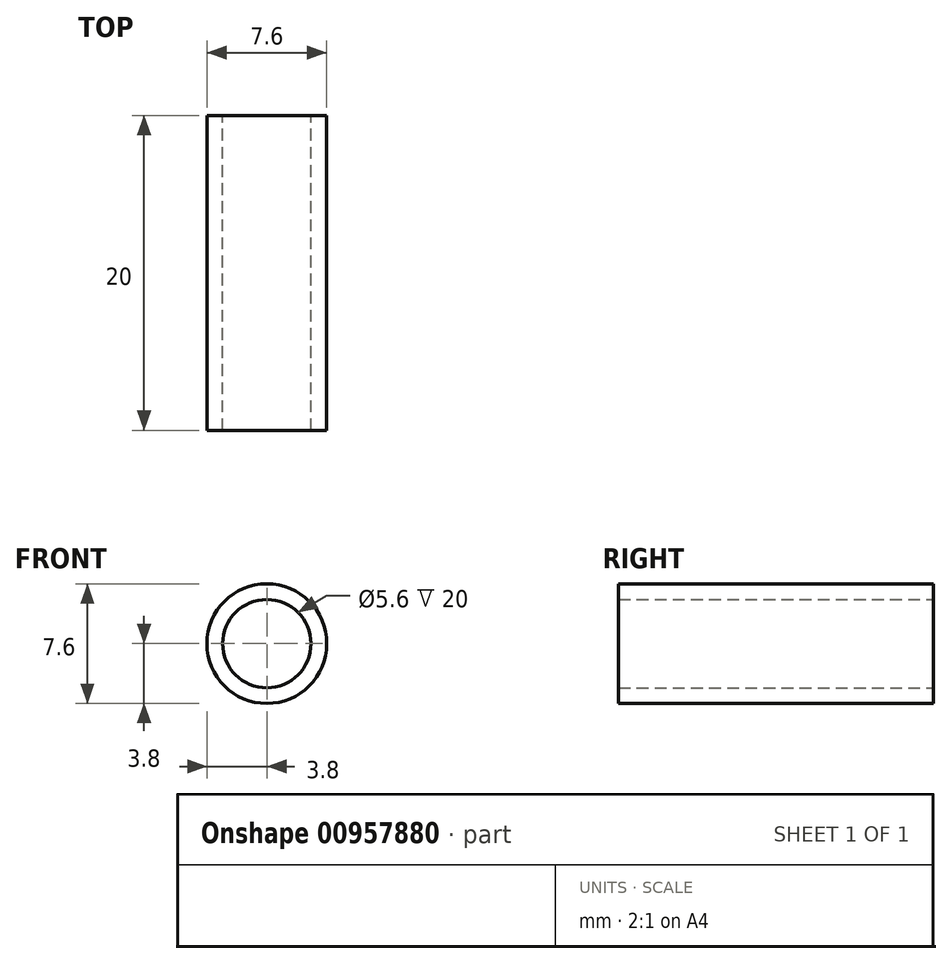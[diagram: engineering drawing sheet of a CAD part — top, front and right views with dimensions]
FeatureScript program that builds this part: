
annotation { "Feature Type Name" : "Feature", "Feature Type Description" : "" }
export const myFeature = defineFeature(function(context is Context, id is Id, definition is map)
    precondition{}
    {
        {
            var Q0;
            Q0=qCreatedBy(makeId("Front.planeOp"),FACE);
            var sketch = newSketch(context, id + "F0", { "sketchPlane" : qUnion([Q0])});
            skCircle(sketch, "E0", {"center": v(0, 0) * mm, "radius": 2.8 * mm});
            skCircle(sketch, "E1", {"center": v(0, 0) * mm, "radius": 3.8 * mm});
            skSolve(sketch);
        }
        {
            var Q0;
            Q0=makeQuery(id+"F0.imprint","IMPRINT",FACE,{"disambiguationData":[TD([[makeQuery(id+"F0.imprint","IMPRINT",EDGE,{"derivedFrom":sQuery(id+"F0.wireOp",EDGE,"E0")}),-1.0]])]});
            extrude(context, id + "F1", {"entities" : qUnion([Q0]), "depth" : 20 * mm, "offsetDistance" : 25 * mm});
        }
    });
